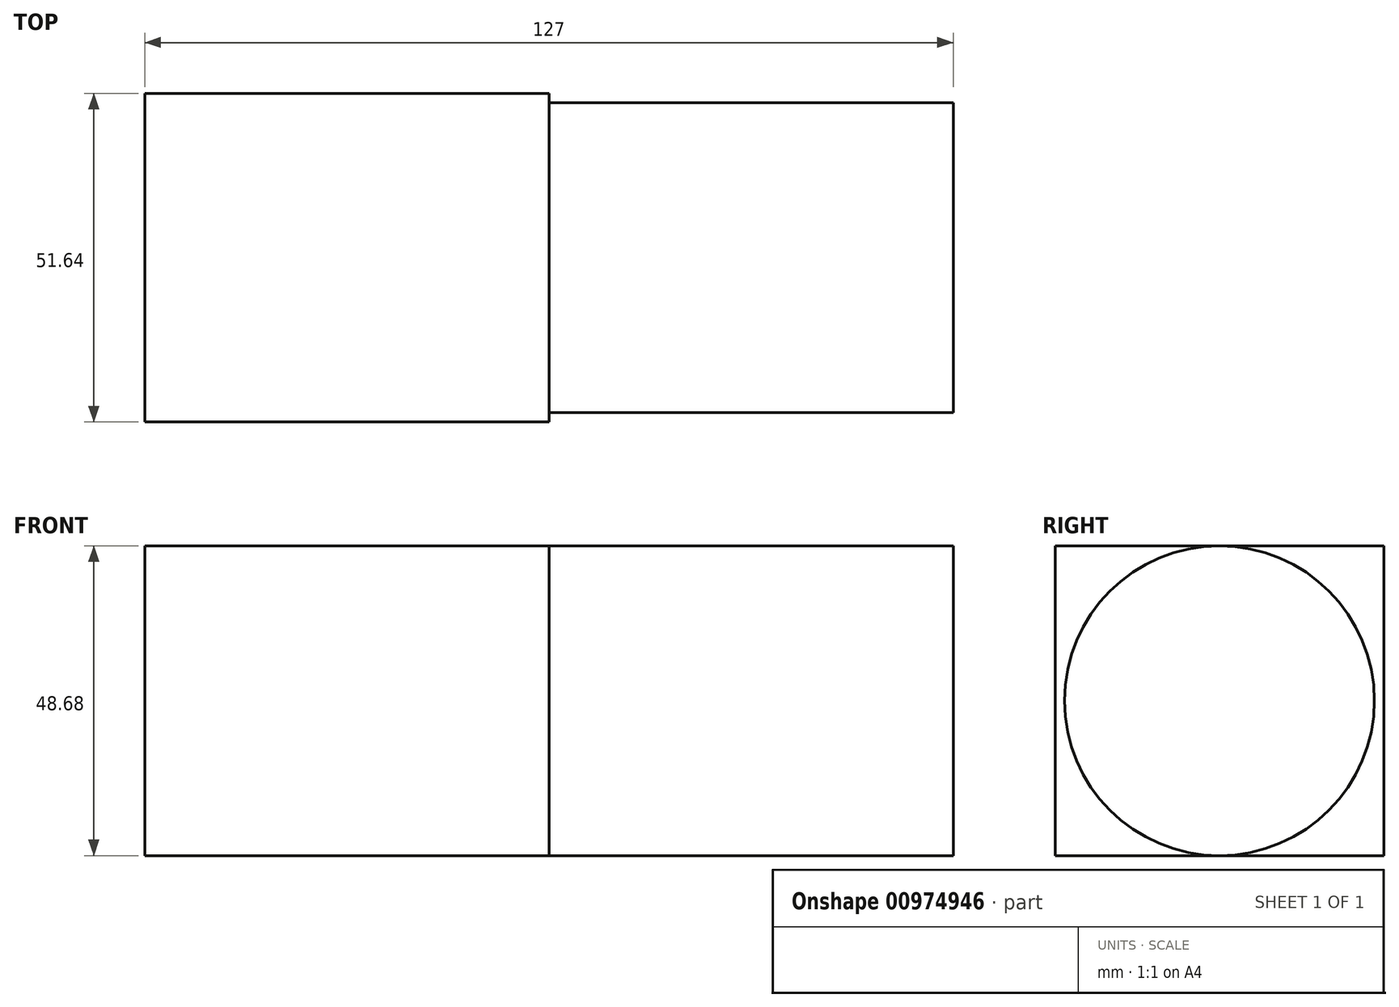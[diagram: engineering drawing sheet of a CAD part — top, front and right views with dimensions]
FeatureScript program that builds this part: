
annotation { "Feature Type Name" : "Feature", "Feature Type Description" : "" }
export const myFeature = defineFeature(function(context is Context, id is Id, definition is map)
    precondition{}
    {
        {
            var Q0;
            Q0=qCreatedBy(makeId("Right.planeOp"),FACE);
            var sketch = newSketch(context, id + "F0", { "sketchPlane" : qUnion([Q0])});
            skLineSegment(sketch, "E0.bottom", {"start": v(51.64, -48.68) * mm, "end": v(0, -48.68) * mm});
            skLineSegment(sketch, "E0.top", {"start": v(51.64, 0) * mm, "end": v(0, 0) * mm});
            skLineSegment(sketch, "E0.left", {"start": v(51.64, -48.68) * mm, "end": v(51.64, 0) * mm});
            skLineSegment(sketch, "E0.right", {"start": v(0, -48.68) * mm, "end": v(0, 0) * mm});
            skSolve(sketch);
        }
        {
            var Q0;
            Q0 = qSketchRegion(id + "F0", true);
            extrude(context, id + "F1", {"entities" : qUnion([Q0]), "depth" : 63.5 * mm, "offsetDistance" : 25.4 * mm});
        }
        {
            var Q0;
            Q0=makeQuery(id+"F1.opExtrude","CAP_FACE",FACE,{"disambiguationData":[OSD([sQuery(id+"F0.wireOp",EDGE,"E0.bottom"),sQuery(id+"F0.wireOp",EDGE,"E0.top"),sQuery(id+"F0.wireOp",EDGE,"E0.left"),sQuery(id+"F0.wireOp",EDGE,"E0.right")])],"isStart":false});
            var sketch = newSketch(context, id + "F2", { "sketchPlane" : qUnion([Q0])});
            skCircle(sketch, "E1", {"center": v(25.82, -24.34) * mm, "radius": 24.34 * mm});
            skPoint(sketch, "E1.centerSnap0", {"position": v(51.64, -24.34) * mm});
            skPoint(sketch, "E1.centerSnap1", {"position": v(25.82, -48.68) * mm});
            skSolve(sketch);
        }
        {
            var Q0;
            {var subQ0=sQuery(id+"F2.wireOp",EDGE,"E1");var subQ1=makeQuery(id+"F2.imprint","INTERSECT",VERTEX,{"derivedFrom":[makeQuery(id+"F1.opExtrude","CAP_EDGE",EDGE,{"disambiguationData":[OSD([sQuery(id+"F0.wireOp",EDGE,"E0.bottom")])],"isStart":false}),subQ0]});Q0=makeQuery(id+"F2.imprint","IMPRINT",FACE,{"disambiguationData":[TD([[makeQuery(id+"F2.imprint","IMPRINT",EDGE,{"disambiguationData":[TD([[subQ1,1.0]])],"derivedFrom":subQ0}),1.0]])]});}
            extrude(context, id + "F3", {"entities" : qUnion([Q0]), "operationType" : NewBodyOperationType.ADD, "depth" : 63.5 * mm, "offsetDistance" : 25.4 * mm});
        }
        {
            var Q0;
            Q0=makeQuery(id+"F3.opExtrude","CAP_FACE",FACE,{"disambiguationData":[OSD([sQuery(id+"F2.wireOp",EDGE,"E1")])],"isStart":false});
            var sketch = newSketch(context, id + "F4", { "sketchPlane" : qUnion([Q0])});
            skSolve(sketch);
        }
        {
            var Q0;
            Q0=makeQuery(id+"F4.imprint","IMPRINT",FACE,{"disambiguationData":[TD([[makeQuery(id+"F4.imprint","IMPRINT",EDGE,{"derivedFrom":makeQuery(id+"F3.opExtrude","CAP_EDGE",EDGE,{"disambiguationData":[OSD([sQuery(id+"F2.wireOp",EDGE,"E1")])],"isStart":false})}),1.0]])]});
            var sketch = newSketch(context, id + "F5", { "sketchPlane" : qUnion([Q0])});
            skEllipse(sketch, "E2", {"center": v(24.2, -24.46) * mm, "majorRadius": 20.86 * mm, "minorRadius": 6.06 * mm, "majorAxis": v(0, 1)});
            skSolve(sketch);
        }
        {
            var Q0;
            Q0=makeQuery(id+"F4.imprint","IMPRINT",FACE,{"disambiguationData":[TD([[makeQuery(id+"F4.imprint","IMPRINT",EDGE,{"derivedFrom":makeQuery(id+"F3.opExtrude","CAP_EDGE",EDGE,{"disambiguationData":[OSD([sQuery(id+"F2.wireOp",EDGE,"E1")])],"isStart":false})}),1.0]])]});
            var Q1;
            Q1=makeQuery(id+"F5.imprint","IMPRINT",FACE,{"disambiguationData":[TD([[makeQuery(id+"F5.imprint","IMPRINT",EDGE,{"derivedFrom":sQuery(id+"F5.wireOp",EDGE,"E2")}),1.0]])]});
            extrude(context, id + "F6", {"entities" : qUnion([Q0, Q1]), "operationType" : NewBodyOperationType.REMOVE, "depth" : 25.4 * mm, "offsetDistance" : 25.4 * mm});
        }
        {
            var Q0;
            Q0=makeQuery(id+"F3.opExtrude","CAP_FACE",FACE,{"disambiguationData":[OSD([sQuery(id+"F2.wireOp",EDGE,"E1")])],"isStart":false});
            var sketch = newSketch(context, id + "F7", { "sketchPlane" : qUnion([Q0])});
            skSolve(sketch);
        }
        {
            var Q0;
            Q0=makeQuery(id+"F7.imprint","IMPRINT",FACE,{"disambiguationData":[TD([[makeQuery(id+"F7.imprint","IMPRINT",EDGE,{"derivedFrom":makeQuery(id+"F3.opExtrude","CAP_EDGE",EDGE,{"disambiguationData":[OSD([sQuery(id+"F2.wireOp",EDGE,"E1")])],"isStart":false})}),1.0]])]});
            var sketch = newSketch(context, id + "F8", { "sketchPlane" : qUnion([Q0])});
            skEllipse(sketch, "E3", {"center": v(30.12, -22.5) * mm, "majorRadius": 21.27 * mm, "minorRadius": 12.54 * mm, "majorAxis": v(-0.68, -0.73)});
            skSolve(sketch);
        }
        {
            var Q0;
            Q0=sQuery(id+"F8.wireOp",EDGE,"E3");
            extrude(context, id + "F9", {"bodyType" : ToolBodyType.SURFACE, "surfaceEntities" : qUnion([Q0]), "depth" : 25.4 * mm, "offsetDistance" : 25.4 * mm});
        }
    });
